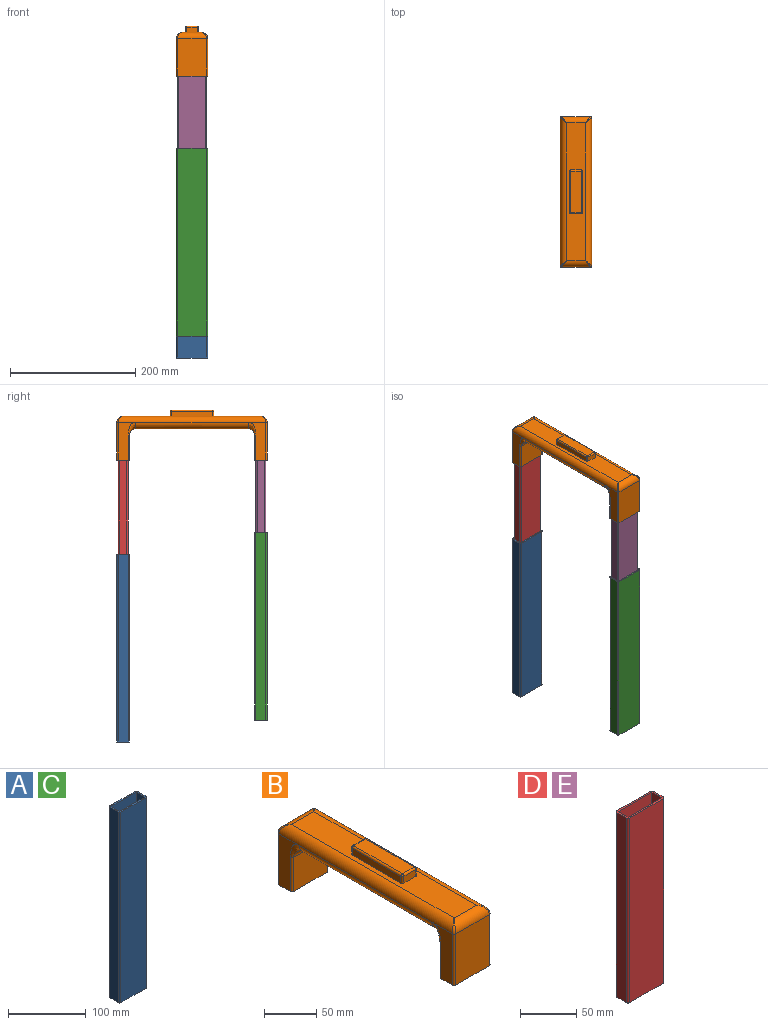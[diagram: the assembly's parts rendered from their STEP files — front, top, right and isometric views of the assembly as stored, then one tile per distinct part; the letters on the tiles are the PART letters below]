
ASSEMBLY  parts=5 mates=4
PART A: 14 faces, bbox 50x20x300 mm
  f0: plane 300x46mm, normal (0,1,0), area 13800mm2, adj f8,f9,f10,f13
  f1: plane 300x16mm, normal (-1,0,0), area 4800mm2, adj f8,f9,f10,f11
  f2: plane 300x46mm, normal (0,-1,0), area 13800mm2, adj f8,f9,f11,f12
  f3: plane 300x16mm, normal (1,0,0), area 4800mm2, adj f4,f6,f8,f9
  f4: plane 300x46mm, normal (0,-1,0), area 13800mm2, adj f3,f5,f8,f9
  f5: plane 300x16mm, normal (-1,0,0), area 4800mm2, adj f4,f6,f8,f9
  f6: plane 300x46mm, normal (0,1,0), area 13800mm2, adj f3,f5,f8,f9
  f7: plane 300x16mm, normal (1,0,0), area 4800mm2, adj f8,f9,f12,f13
  f8: plane 50x20mm, normal (0,0,1), area 260.6mm2, adj f0,f1,f2,f3,f4,f5,f6,f7
  f9: plane 50x20mm, normal (0,0,-1), area 260.6mm2, adj f0,f1,f2,f3,f4,f5,f6,f7
  f10: cylinder r=2mm len=300mm, axis (0,0,1), area 942.5mm2, adj f0,f1,f8,f9
  f11: cylinder r=2mm len=300mm, axis (0,0,-1), area 942.5mm2, adj f1,f2,f8,f9
  f12: cylinder r=2mm len=300mm, axis (0,0,1), area 942.5mm2, adj f2,f7,f8,f9
  f13: cylinder r=2mm len=300mm, axis (0,0,-1), area 942.5mm2, adj f0,f7,f8,f9
PART B: 63 faces, bbox 50.6x240.6x80.6 mm
  f0: plane 60.63x28.63mm, normal (1,0,0), area 1001.6mm2, adj f11,f28,f29,f32,f41
  f1: plane 60.63x28.63mm, normal (-1,0,0), area 1001.6mm2, adj f20,f22,f24,f35,f42
  f2: plane 180x30mm, normal (0,0,-1), area 5400mm2, adj f30,f31,f37,f40
  f3: plane 60x46mm, normal (0,1,0), area 2760mm2, adj f11,f26,f29,f45
  f4: plane 60.64x28.64mm, normal (-1,0,0), area 1001.6mm2, adj f11,f26,f27,f36,f42
  f5: plane 46x40mm, normal (0,-1,0), area 1840mm2, adj f11,f27,f28,f31
  f6: plane 50x16mm, normal (1,0,0), area 800mm2, adj f7,f9,f11,f14
  f7: plane 50x46mm, normal (0,-1,0), area 2300mm2, adj f6,f8,f11,f14
  f8: plane 50x16mm, normal (-1,0,0), area 800mm2, adj f7,f9,f11,f14
  f9: plane 50x46mm, normal (0,1,0), area 2300mm2, adj f6,f8,f11,f14
  f10: plane 60.64x28.64mm, normal (1,0,0), area 1001.6mm2, adj f20,f23,f25,f33,f41
  f11: plane 50x20mm, normal (0,0,-1), area 260.6mm2, adj f0,f3,f4,f5,f6,f7,f8,f9
  f12: plane 60x46mm, normal (0,-1,0), area 2760mm2, adj f20,f24,f25,f34
  f13: plane 220x30mm, normal (0,0,1), area 5203.4mm2, adj f34,f41,f42,f45,f46,f47,f48,f49
  f14: plane 46x16mm, normal (0,0,-1), area 736mm2, adj f6,f7,f8,f9
  f15: plane 46x40mm, normal (0,1,0), area 1840mm2, adj f20,f22,f23,f30
  f16: plane 50x16mm, normal (1,0,0), area 800mm2, adj f17,f19,f20,f21
  f17: plane 50x46mm, normal (0,1,0), area 2300mm2, adj f16,f18,f20,f21
  f18: plane 50x16mm, normal (-1,0,0), area 800mm2, adj f17,f19,f20,f21
  f19: plane 50x46mm, normal (0,-1,0), area 2300mm2, adj f16,f18,f20,f21
  f20: plane 50x20mm, normal (0,0,-1), area 260.6mm2, adj f1,f10,f12,f15,f16,f17,f18,f19
  f21: plane 46x16mm, normal (0,0,-1), area 736mm2, adj f16,f17,f18,f19
  f22: cylinder r=2mm len=40mm, axis (0,0,1), area 125.7mm2, adj f1,f15,f20,f35
  f23: cylinder r=2mm len=40mm, axis (0,0,-1), area 125.7mm2, adj f10,f15,f20,f33
  f24: cylinder r=2mm len=60mm, axis (0,0,1), area 188.5mm2, adj f1,f12,f20,f39
  f25: cylinder r=2mm len=60mm, axis (0,0,-1), area 188.5mm2, adj f10,f12,f20,f38
  f26: cylinder r=2mm len=60mm, axis (0,0,1), area 188.5mm2, adj f3,f4,f11,f44
  f27: cylinder r=2mm len=40mm, axis (0,0,-1), area 125.7mm2, adj f4,f5,f11,f36
  f28: cylinder r=2mm len=40mm, axis (0,0,1), area 125.7mm2, adj f0,f5,f11,f32
  f29: cylinder r=2mm len=60mm, axis (0,0,-1), area 188.5mm2, adj f0,f3,f11,f43
  f30: cylinder r=10mm len=46mm, axis (1,0,0), area 596.9mm2, adj f2,f15,f33,f35
  f31: cylinder r=10mm len=46mm, axis (1,0,0), area 596.9mm2, adj f2,f5,f32,f36
  f32: bspline ~20x12mm, area 176.7mm2, adj f0,f28,f31,f37
  f33: bspline ~20x12mm, area 176.7mm2, adj f10,f23,f30,f37
  f34: cylinder r=10mm len=46mm, axis (1,0,0), area 596.9mm2, adj f12,f13,f38,f39
  f35: bspline ~20x12mm, area 176.7mm2, adj f1,f22,f30,f40
  f36: bspline ~20x12mm, area 176.7mm2, adj f4,f27,f31,f40
  f37: cylinder r=10mm len=180mm, axis (0,1,0), area 2827.4mm2, adj f2,f32,f33,f41
  f38: bspline ~10.39x10mm, area 21.6mm2, adj f25,f34,f41
  f39: bspline ~10.39x10mm, area 21.6mm2, adj f24,f34,f42
  f40: cylinder r=10mm len=180mm, axis (0,-1,0), area 2827.4mm2, adj f2,f35,f36,f42
  f41: cylinder r=10mm len=236mm, axis (0,-1,0), area 3581.4mm2, adj f0,f10,f13,f37,f38,f43
  f42: cylinder r=10mm len=236mm, axis (0,1,0), area 3581.4mm2, adj f1,f4,f13,f39,f40,f44
  f43: bspline ~10.39x10mm, area 21.6mm2, adj f29,f41,f45
  f44: bspline ~10.39x10mm, area 21.6mm2, adj f26,f42,f45
  f45: cylinder r=10mm len=46mm, axis (1,0,0), area 596.9mm2, adj f3,f13,f43,f44
  f46: plane 16x8mm, normal (0,1,0), area 128mm2, adj f13,f53,f59,f62
  f47: plane 66x8mm, normal (-1,0,0), area 528mm2, adj f13,f56,f60,f62
  f48: plane 16x8mm, normal (0,-1,0), area 128mm2, adj f13,f51,f55,f56
  f49: plane 66x8mm, normal (1,0,0), area 528mm2, adj f13,f51,f53,f54
  f50: plane 66x16mm, normal (0,0,1), area 1056mm2, adj f54,f55,f59,f60
  f51: cylinder r=2mm len=8mm, axis (0,0,1), area 25.1mm2, adj f13,f48,f49,f52
  f52: sphere r=2mm, area 6.3mm2, adj f51,f54,f55
  f53: cylinder r=2mm len=8mm, axis (0,0,-1), area 25.1mm2, adj f13,f46,f49,f57
  f54: cylinder r=2mm len=66mm, axis (0,-1,0), area 207.3mm2, adj f49,f50,f52,f57
  f55: cylinder r=2mm len=16mm, axis (-1,0,0), area 50.3mm2, adj f48,f50,f52,f58
  f56: cylinder r=2mm len=8mm, axis (0,0,-1), area 25.1mm2, adj f13,f47,f48,f58
  f57: sphere r=2mm, area 8.6mm2, adj f53,f54,f59
  f58: sphere r=2mm, area 6.3mm2, adj f55,f56,f60
  f59: cylinder r=2mm len=16mm, axis (1,0,0), area 50.3mm2, adj f46,f50,f57,f61
  f60: cylinder r=2mm len=66mm, axis (0,1,0), area 207.3mm2, adj f47,f50,f58,f61
  f61: sphere r=2mm, area 8.6mm2, adj f59,f60,f62
  f62: cylinder r=2mm len=8mm, axis (0,0,1), area 25.1mm2, adj f13,f46,f47,f61
PART C: same geometry as A
PART D: 14 faces, bbox 46x16x200 mm
  f0: plane 200x42mm, normal (0,1,0), area 8400mm2, adj f8,f9,f10,f13
  f1: plane 200x12mm, normal (-1,0,0), area 2400mm2, adj f8,f9,f10,f11
  f2: plane 200x42mm, normal (0,-1,0), area 8400mm2, adj f8,f9,f11,f12
  f3: plane 200x12mm, normal (1,0,0), area 2400mm2, adj f4,f6,f8,f9
  f4: plane 200x42mm, normal (0,-1,0), area 8400mm2, adj f3,f5,f8,f9
  f5: plane 200x12mm, normal (-1,0,0), area 2400mm2, adj f4,f6,f8,f9
  f6: plane 200x42mm, normal (0,1,0), area 8400mm2, adj f3,f5,f8,f9
  f7: plane 200x12mm, normal (1,0,0), area 2400mm2, adj f8,f9,f12,f13
  f8: plane 46x16mm, normal (0,0,1), area 228.6mm2, adj f0,f1,f2,f3,f4,f5,f6,f7
  f9: plane 46x16mm, normal (0,0,-1), area 228.6mm2, adj f0,f1,f2,f3,f4,f5,f6,f7
  f10: cylinder r=2mm len=200mm, axis (0,0,1), area 628.3mm2, adj f0,f1,f8,f9
  f11: cylinder r=2mm len=200mm, axis (0,0,-1), area 628.3mm2, adj f1,f2,f8,f9
  f12: cylinder r=2mm len=200mm, axis (0,0,1), area 628.3mm2, adj f2,f7,f8,f9
  f13: cylinder r=2mm len=200mm, axis (0,0,-1), area 628.3mm2, adj f0,f7,f8,f9
PART E: same geometry as D
PLACE A t=(-131,70,-450)mm
PLACE B t=(-131,70,0)mm fixed
PLACE C t=(-131,-150,-415)mm
PLACE D t=(-131,70,-150)mm
PLACE E t=(-131,-150,-185)mm
MATE slider D.f8 <-> B.f14  axis (0,0,1) through (-131,70,50)mm
MATE slider C.f8 <-> E.f9  axis (0,0,1) through (-131,-150,-115)mm
MATE slider E.f8 <-> B.f21  axis (0,0,1) through (-131,-150,15)mm
MATE slider A.f8 <-> D.f9  axis (0,0,1) through (-131,70,-150)mm
